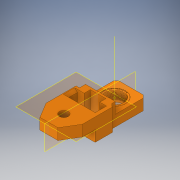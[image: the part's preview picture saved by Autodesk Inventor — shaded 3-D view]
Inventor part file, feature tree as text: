
AUTODESK INVENTOR PART (.ipt)
format: ipt  version: 2019 (Build 230136000, 136)  size: 1,151,488 bytes
history: native  units: mm
features: other x19, reference x16, extrude x11, sketch x11, projected_geometry x4, plane x2, mirror x1, hole x1, chamfer x1
ambient origin geometry x8: Origin, YZ Plane, XZ Plane, XY Plane, X Axis, Y Axis, Z Axis, Center Point
bodies: Solid2 (feature_tree)
feature tree (66):
  plane  "Work Plane8"
  extrude  "Extrusion11"  TaperAngle=0.0deg  [1 undecoded]
  extrude  "Extrusion12"  Depth=4.0mm TaperAngle=0.0deg
  mirror  "Mirror3"
  extrude  "Extrusion16"  Depth=10.0mm TaperAngle=0.0deg
  extrude  "Extrusion17"  Depth=10.0mm TaperAngle=0.0deg
  hole  "Hole1"  [1 undecoded]
  extrude  "Extrusion19"  TaperAngle=0.0deg  [1 undecoded]
  extrude  "Extrusion20"  Depth=1.5mm
  extrude  "Extrusion22"  Depth=3.0mm
  other  "Arbeitsachse1"
  other  "Arbeitspunkt1"
  plane  "Arbeitsebene10"
  extrude  "Extrusion23"  Depth=10.0mm TaperAngle=0.0deg
  extrude  "Extrusion24"  Depth=1.0mm
  chamfer  "Fase4"  Distance=1.0mm
  extrude  "Extrusion25"  Depth=3.0mm
  extrude  "Extrusion26"  Depth=10.0mm TaperAngle=0.0deg
  other  "Spirale3"
  sketch  "Sketch12"  dims[d64=180.0deg d66=-10.0mm d67=0.0mm]
  reference  "Reference33"
  reference  "Reference35"
  reference  "Reference36"
  reference  "Reference42"
  sketch  "Sketch17"  dims[d70=10.0mm d71=0.0mm d83=4.0mm d84=0.0mm]
  reference  "Reference44"
  reference  "Reference45"
  reference  "Reference46"
  sketch  "Sketch19"  dims[d86=10.0mm d87=0.0mm]
  sketch  "Sketch21"  dims[d89=3.2mm d90=6.0mm d91=6.0mm d92=22.0mm d93=90.0deg d94=8.0mm d95=20.594885mm d101=10.0mm d102=0.0mm]
  sketch  "Sketch22"  dims[d103=8.0mm d104=10.0mm d105=0.0mm]
  reference  "Reference55"
  reference  "Reference58"
  reference  "Reference59"
  reference  "Referenz68"
  reference  "Referenz69"
  projected_geometry  "Projizierte Kontur11"
  reference  "Referenz71"
  sketch  "Skizze25"  dims[d110=0.3mm d111=0.3mm]
  reference  "Referenz72"
  reference  "Referenz73"
  other  "Arbeitsachse2"
  sketch  "Skizze27"  dims[d118=0.0mm d119=0.0mm]
  projected_geometry  "Projizierte Kontur12"
  sketch  "Skizze28"  dims[d120=10.0mm d121=0.0mm d139=1.5mm]
  reference  "Referenz74"
  sketch  "Skizze29"  dims[d140=10.0mm d141=0.0mm d142=3.0mm]
  projected_geometry  "Projizierte Kontur13"
  projected_geometry  "Projizierte Kontur14"
  sketch  "Skizze31"  dims[d143=3.0mm d144=10.0mm d145=0.0mm]
  sketch  "Skizze32"  dims[d146=2.5mm d147=2.0mm d148=45.0deg d149=1.0mm d150=1.0mm d151=3.0mm d152=10.0mm d153=0.0mm d169=2.0mm d170=10.0mm d171=0.0mm d176=0.15mm d177=360.0deg d178=120.0deg d179=0.15mm d180=120.0deg d181=1.0mm d182=0.713333mm d183=0.721mm d184=10.0mm d185=130.0mm d186=0.0mm d187=90.0deg d188=90.0deg d189=0.0mm d190=0.0mm d191=9.95mm d192=0.72mm]
  other  "Assembly_Cube_Z_Focus_Drylin_NEMA_v3.iam"
  other  "30_Cube_Z_Focus_MGN_NEMA_adapter:1"
  other  "30_Cube_Z_Focus_Drylin_NEMA_base_v3:1"
  other  "Assembly_Cube_Z_Focus_Drylin_NEMA_slide.iam"
  other  "30_Cube_Z_Focus_Drylin_NEMA_slide_part1:1"
  other  "30_Cube_Z_Focus_Drylin_NEMA_slide_part2:1"
  other  "Assembly_Cube_Z_Focus_MGN_NEMA_v3.iam"
  other  "DIN 912 - replaced by DIN EN ISO 4762 M3 x 30:1"
  other  "00_MGN12H, LINEAR GUIDE BLOCK:1"
  other  "<userpath>\Downloads\cellSTORM\cellSTORM_v5_microsocpe.iam"
  other  "cellSTORM_v5_microsocpe.iam"
  other  "30_Cube_Z_Focus_MGN_NEMA_rail:1"
  other  "30_Cube_Z_Focus_MGN_NEMA_adapter_RMS:1"
  other  "cellSTORM_lightpath:1"
  other  "cellSTORM_v5_opticalstage:1"
note: 3 required parameter values undecoded (feature->parameter linkage not recoverable at this tier; creation-order binding heuristic only, values carry confidence <= 0.55)
